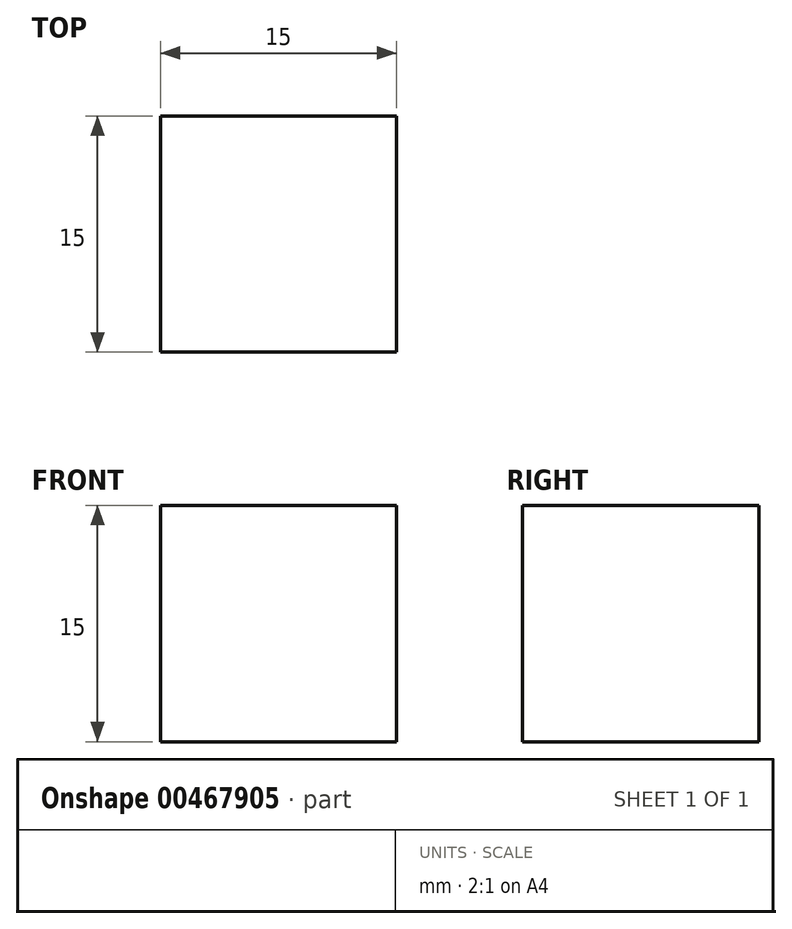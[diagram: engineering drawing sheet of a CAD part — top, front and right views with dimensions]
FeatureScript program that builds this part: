
annotation { "Feature Type Name" : "Feature", "Feature Type Description" : "" }
export const myFeature = defineFeature(function(context is Context, id is Id, definition is map)
    precondition{}
    {
        {
            var Q0;
            Q0=qCreatedBy(makeId("Top.planeOp"),FACE);
            var sketch = newSketch(context, id + "F0", { "sketchPlane" : qUnion([Q0])});
            skLineSegment(sketch, "E0.bottom", {"start": v(-15, -15) * mm, "end": v(0, -15) * mm});
            skLineSegment(sketch, "E0.top", {"start": v(-15, 0) * mm, "end": v(0, 0) * mm});
            skLineSegment(sketch, "E0.left", {"start": v(-15, -15) * mm, "end": v(-15, 0) * mm});
            skLineSegment(sketch, "E0.right", {"start": v(0, -15) * mm, "end": v(0, 0) * mm});
            skSolve(sketch);
        }
        {
            var Q0;
            Q0=makeQuery(id+"F0.imprint","IMPRINT",FACE,{"disambiguationData":[TD([[makeQuery(id+"F0.imprint","IMPRINT",EDGE,{"derivedFrom":sQuery(id+"F0.wireOp",EDGE,"E0.bottom")}),1.0]])]});
            extrude(context, id + "F1", {"entities" : qUnion([Q0]), "depth" : 15 * mm});
        }
    });
